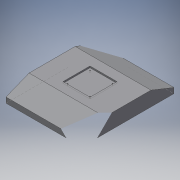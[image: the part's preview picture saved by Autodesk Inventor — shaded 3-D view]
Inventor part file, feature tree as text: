
AUTODESK INVENTOR PART (.ipt)
format: ipt  version: 2016 (Build 200138000, 138)  size: 126,464 bytes
history: native  units: in
note: dims shown in document units (in); Inventor stores cm internally (conversion verified against a paired STEP export)
features: extrude x4, sketch x4
ambient origin geometry x8: Origin, YZ Plane, XZ Plane, XY Plane, X Axis, Y Axis, Z Axis, Center Point
bodies: Solid1 (feature_tree)
feature tree (8):
  extrude  "Extrusion1"  Depth=13.3in
  extrude  "Extrusion2"  Depth=2.56in
  extrude  "Extrusion3"  Depth=0.94in
  extrude  "Extrusion4"  Depth=4.75in
  sketch  "Sketch1"  dims[d0=16.2in d1=13.3in]
  sketch  "Sketch2"  dims[d2=2.56in d3=0.0in d4=8.1in]
  sketch  "Sketch3"  dims[d5=0.94in d6=0.94in]
  sketch  "Sketch4"  dims[d7=15.2475in d8=0.0in d9=4.75in d10=4.75in d11=0.2812in d12=0.0in d13=0.125in d14=0.125in d15=0.125in d16=0.125in d17=3.937in d18=3.937in d19=3.937in d20=0.3in d21=0.0in]
